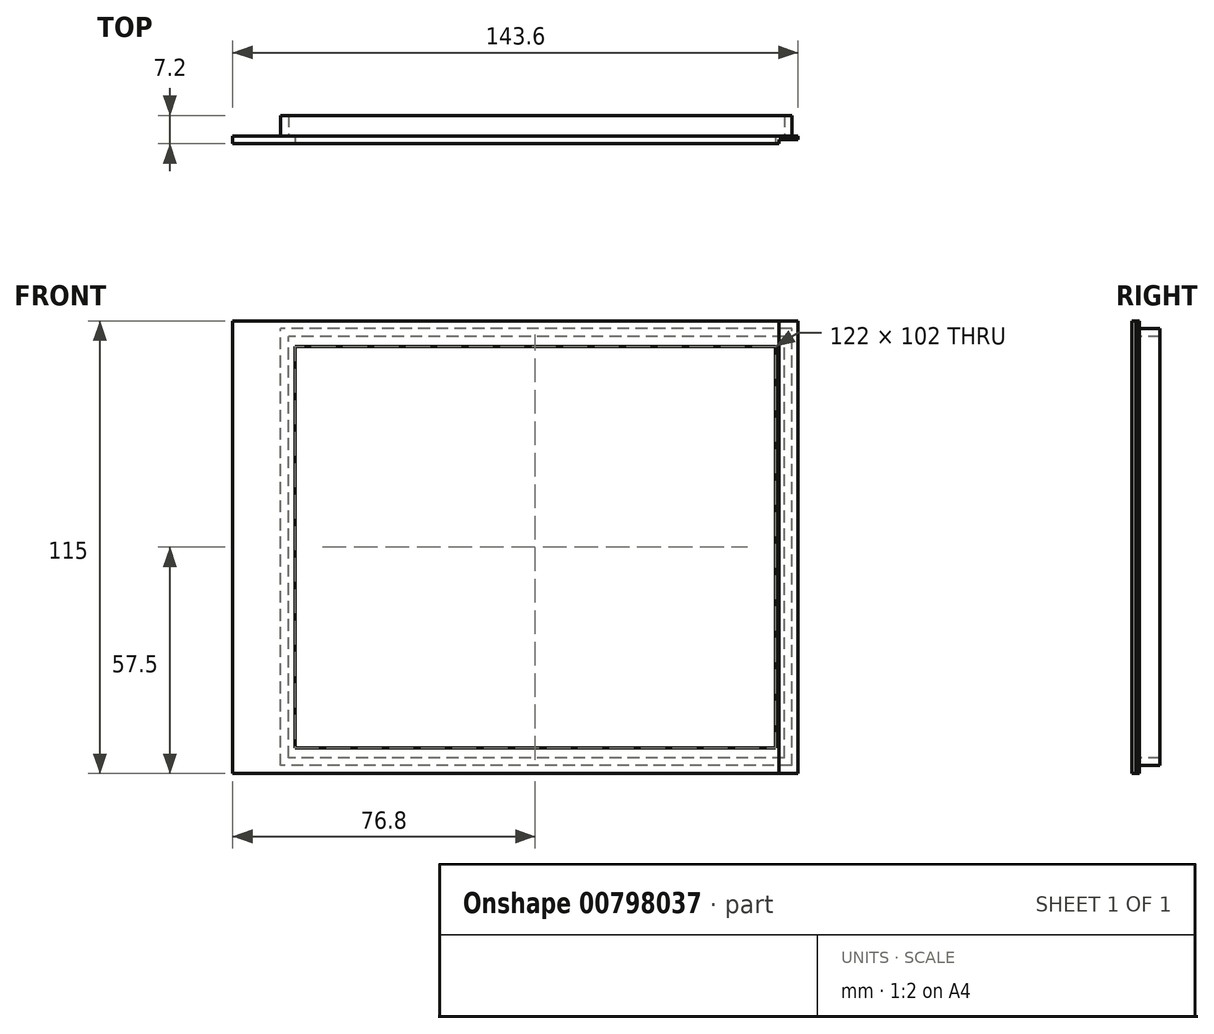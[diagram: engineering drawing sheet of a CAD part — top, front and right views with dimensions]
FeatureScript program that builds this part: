
annotation { "Feature Type Name" : "Feature", "Feature Type Description" : "" }
export const myFeature = defineFeature(function(context is Context, id is Id, definition is map)
    precondition{}
    {
        {
            var Q0;
            Q0=qCreatedBy(makeId("Front.planeOp"),FACE);
            var sketch = newSketch(context, id + "F0", { "sketchPlane" : qUnion([Q0])});
            skLineSegment(sketch, "E0.bottom", {"start": v(51.5, -39) * mm, "end": v(-51.5, -39) * mm, "construction": true});
            skLineSegment(sketch, "E0.top", {"start": v(51.5, 39) * mm, "end": v(-51.5, 39) * mm, "construction": true});
            skLineSegment(sketch, "E0.left", {"start": v(51.5, -39) * mm, "end": v(51.5, 39) * mm, "construction": true});
            skLineSegment(sketch, "E0.right", {"start": v(-51.5, -39) * mm, "end": v(-51.5, 39) * mm, "construction": true});
            skLineSegment(sketch, "E1.bottom", {"start": v(-61.3, 51) * mm, "end": v(60.7, 51) * mm});
            skLineSegment(sketch, "E1.top", {"start": v(-61.3, -51) * mm, "end": v(60.7, -51) * mm});
            skLineSegment(sketch, "E1.left", {"start": v(-61.3, 51) * mm, "end": v(-61.3, -51) * mm});
            skLineSegment(sketch, "E1.right", {"start": v(60.7, 51) * mm, "end": v(60.7, -51) * mm});
            skPoint(sketch, "E2.middle", {"position": v(0, 0) * mm});
            skLineSegment(sketch, "E3.bottom", {"start": v(66.5, -57.5) * mm, "end": v(-77.1, -57.5) * mm});
            skLineSegment(sketch, "E3.top", {"start": v(66.5, 57.5) * mm, "end": v(-77.1, 57.5) * mm});
            skLineSegment(sketch, "E3.left", {"start": v(66.5, -57.5) * mm, "end": v(66.5, 57.5) * mm});
            skLineSegment(sketch, "E3.right", {"start": v(-77.1, -57.5) * mm, "end": v(-77.1, 57.5) * mm});
            skPoint(sketch, "E3.middle", {"position": v(-5.3, 0) * mm});
            skLineSegment(sketch, "E4.bottom", {"start": v(65, -55.5) * mm, "end": v(-65, -55.5) * mm});
            skLineSegment(sketch, "E4.top", {"start": v(65, 55.5) * mm, "end": v(-65, 55.5) * mm});
            skLineSegment(sketch, "E4.left", {"start": v(65, -55.5) * mm, "end": v(65, 55.5) * mm});
            skLineSegment(sketch, "E4.right", {"start": v(-65, -55.5) * mm, "end": v(-65, 55.5) * mm});
            skLineSegment(sketch, "E5.0", {"start": v(63, 53.5) * mm, "end": v(-63, 53.5) * mm});
            skLineSegment(sketch, "E5.1", {"start": v(63, -53.5) * mm, "end": v(63, 53.5) * mm});
            skLineSegment(sketch, "E5.2", {"start": v(63, -53.5) * mm, "end": v(-63, -53.5) * mm});
            skLineSegment(sketch, "E5.3", {"start": v(-63, -53.5) * mm, "end": v(-63, 53.5) * mm});
            skLineSegment(sketch, "E6.bottom", {"start": v(66.5, 57.5) * mm, "end": v(61.7, 57.5) * mm});
            skLineSegment(sketch, "E6.right", {"start": v(61.7, 57.5) * mm, "end": v(61.7, -57.5) * mm});
            skLineSegment(sketch, "E7", {"start": v(61.7, -57.5) * mm, "end": v(66.5, -57.5) * mm});
            skSolve(sketch);
        }
        {
            var Q0;
            Q0=makeQuery(id+"F0.imprint","IMPRINT",FACE,{"disambiguationData":[TD([[makeQuery(id+"F0.imprint","IMPRINT",EDGE,{"derivedFrom":sQuery(id+"F0.wireOp",EDGE,"E3.bottom")}),-1.0]])]});
            var Q1;
            Q1=makeQuery(id+"F0.imprint","IMPRINT",FACE,{"disambiguationData":[TD([[makeQuery(id+"F0.imprint","IMPRINT",EDGE,{"derivedFrom":sQuery(id+"F0.wireOp",EDGE,"E4.bottom")}),-1.0]])]});
            var Q2;
            Q2=makeQuery(id+"F0.imprint","IMPRINT",FACE,{"disambiguationData":[TD([[makeQuery(id+"F0.imprint","IMPRINT",EDGE,{"derivedFrom":sQuery(id+"F0.wireOp",EDGE,"E1.bottom")}),1.0]])]});
            var Q3;
            {var subQ0=sQuery(id+"F0.wireOp",EDGE,"E4.left");Q3=makeQuery(id+"F0.imprint","IMPRINT",FACE,{"disambiguationData":[TD([[makeQuery(id+"F0.imprint","IMPRINT",EDGE,{"derivedFrom":subQ0}),-1.0]])]});}
            var Q4;
            {var subQ0=sQuery(id+"F0.wireOp",EDGE,"E5.1");Q4=makeQuery(id+"F0.imprint","IMPRINT",FACE,{"disambiguationData":[TD([[makeQuery(id+"F0.imprint","IMPRINT",EDGE,{"derivedFrom":subQ0}),1.0]])]});}
            extrude(context, id + "F1", {"entities" : qUnion([Q0, Q1, Q2, Q3, Q4]), "oppositeDirection" : true, "depth" : 2 * mm, "offsetDistance" : 25 * mm});
        }
        {
            var Q0;
            Q0=makeQuery(id+"F0.imprint","IMPRINT",FACE,{"disambiguationData":[TD([[makeQuery(id+"F0.imprint","IMPRINT",EDGE,{"derivedFrom":sQuery(id+"F0.wireOp",EDGE,"E4.bottom")}),-1.0]])]});
            extrude(context, id + "F2", {"entities" : qUnion([Q0]), "operationType" : NewBodyOperationType.ADD, "oppositeDirection" : true, "depth" : 7.2 * mm, "offsetDistance" : 25 * mm});
        }
        {
            var Q0;
            {var subQ0=sQuery(id+"F0.wireOp",EDGE,"E4.left");Q0=makeQuery(id+"F0.imprint","IMPRINT",FACE,{"disambiguationData":[TD([[makeQuery(id+"F0.imprint","IMPRINT",EDGE,{"derivedFrom":subQ0}),-1.0]])]});}
            var Q1;
            {var subQ0=sQuery(id+"F0.wireOp",EDGE,"E5.1");Q1=makeQuery(id+"F0.imprint","IMPRINT",FACE,{"disambiguationData":[TD([[makeQuery(id+"F0.imprint","IMPRINT",EDGE,{"derivedFrom":subQ0}),1.0]])]});}
            var Q2;
            {var subQ8=sQuery(id+"F0.wireOp",EDGE,"E4.left");Q2=makeQuery(id+"F0.imprint","IMPRINT",FACE,{"disambiguationData":[TD([[makeQuery(id+"F0.imprint","IMPRINT",EDGE,{"derivedFrom":subQ8}),1.0]])]});}
            extrude(context, id + "F3", {"entities" : qUnion([Q0, Q1, Q2]), "operationType" : NewBodyOperationType.REMOVE, "oppositeDirection" : true, "depth" : 1 * mm, "offsetDistance" : 25 * mm, "hasSecondDirection" : true, "secondDirectionOppositeDirection" : false, "secondDirectionDepth" : 2 * mm});
        }
    });
